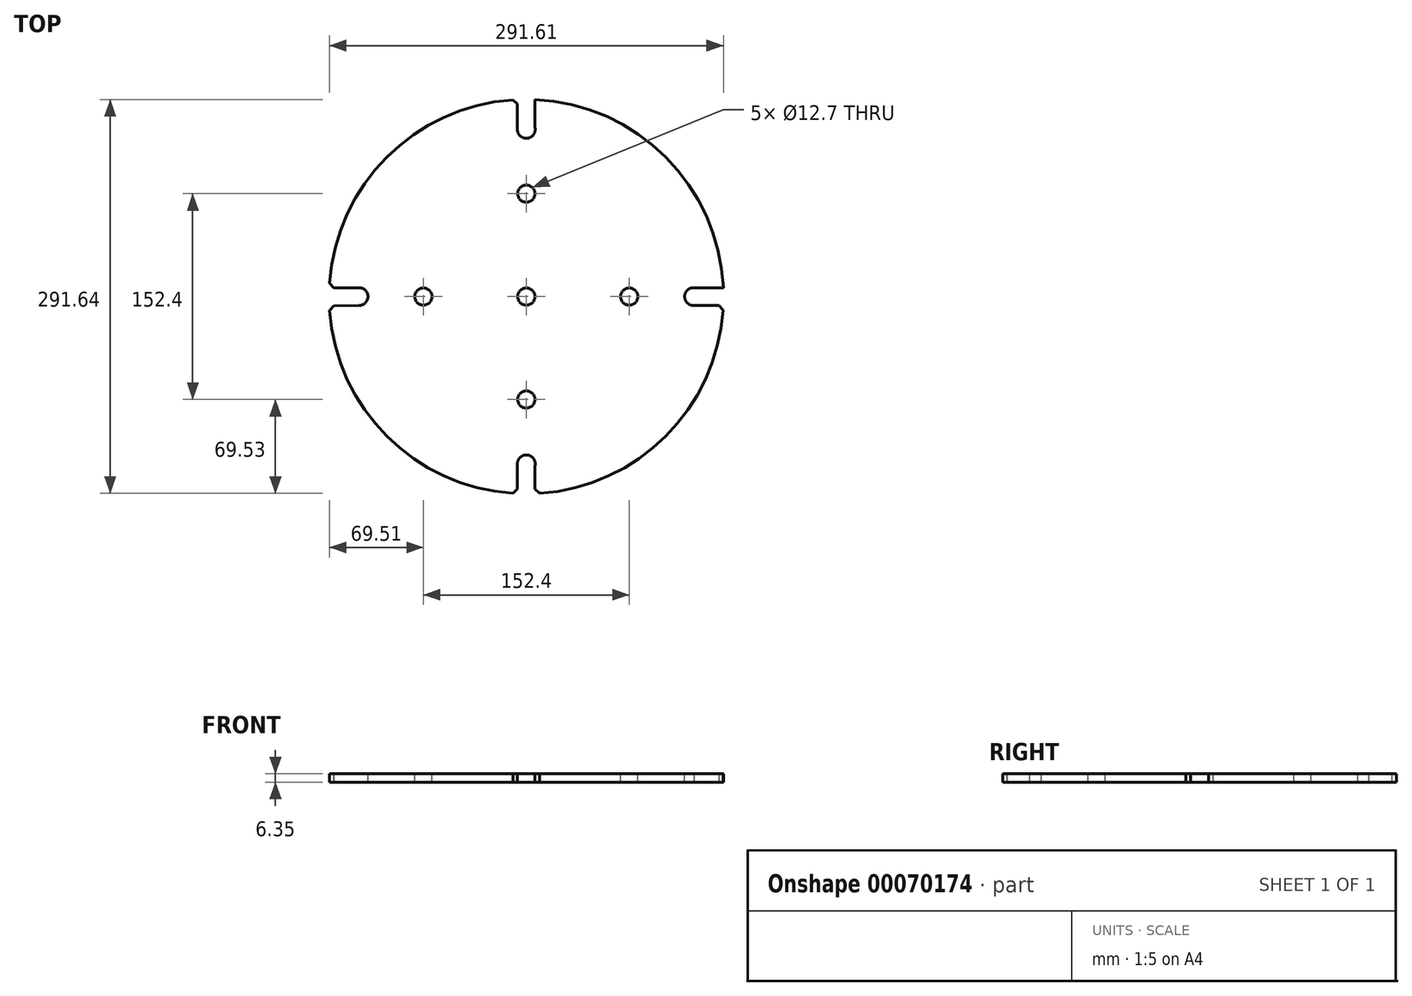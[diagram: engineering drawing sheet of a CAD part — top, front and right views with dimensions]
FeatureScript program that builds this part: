
annotation { "Feature Type Name" : "Feature", "Feature Type Description" : "" }
export const myFeature = defineFeature(function(context is Context, id is Id, definition is map)
    precondition{}
    {
        {
            var Q0;
            Q0=qCreatedBy(makeId("Top.planeOp"),FACE);
            var sketch = newSketch(context, id + "F0", { "sketchPlane" : qUnion([Q0])});
            skCircle(sketch, "E0", {"center": v(0, 0) * mm, "radius": 146.05 * mm});
            skSolve(sketch);
        }
        {
            var Q0;
            Q0 = qSketchRegion(id + "F0", true);
            extrude(context, id + "F1", {"entities" : qUnion([Q0]), "depth" : 6.35 * mm});
        }
        {
            var Q0;
            Q0=makeQuery(id+"F1.opExtrude","CAP_FACE",FACE,{"disambiguationData":[OSD([sQuery(id+"F0.wireOp",EDGE,"E0")])],"isStart":false});
            var sketch = newSketch(context, id + "F2", { "sketchPlane" : qUnion([Q0])});
            skCircle(sketch, "E1", {"center": v(0, 123.83) * mm, "radius": 6.6 * mm});
            skLineSegment(sketch, "E2", {"start": v(6.43, 125.34) * mm, "end": v(6.43, 145.9) * mm});
            skLineSegment(sketch, "E3", {"start": v(-6.6, 123.83) * mm, "end": v(-6.6, 145.9) * mm});
            skCircle(sketch, "E4", {"center": v(-123.83, 0) * mm, "radius": 6.6 * mm});
            skCircle(sketch, "E5", {"center": v(123.83, 0) * mm, "radius": 6.6 * mm});
            skCircle(sketch, "E6", {"center": v(0, -123.83) * mm, "radius": 6.6 * mm});
            skLineSegment(sketch, "E7", {"start": v(-123.8, 6.6) * mm, "end": v(-145.9, 6.6) * mm});
            skLineSegment(sketch, "E8", {"start": v(-123.74, -6.6) * mm, "end": v(-145.89, -6.88) * mm});
            skLineSegment(sketch, "E9", {"start": v(123.83, 6.6) * mm, "end": v(145.9, 6.6) * mm});
            skLineSegment(sketch, "E10", {"start": v(124.53, -6.57) * mm, "end": v(145.9, -6.57) * mm});
            skLineSegment(sketch, "E11", {"start": v(-6.6, -123.8) * mm, "end": v(-6.6, -145.9) * mm});
            skLineSegment(sketch, "E12", {"start": v(6.34, -125.67) * mm, "end": v(6.34, -145.91) * mm});
            skSolve(sketch);
        }
        {
            var Q0;
            {var subQ0=sQuery(id+"F2.wireOp",EDGE,"E1");var subQ1=makeQuery(id+"F2.imprint","INTERSECT",VERTEX,{"derivedFrom":[subQ0,sQuery(id+"F2.wireOp",EDGE,"E2")]});Q0=makeQuery(id+"F2.imprint","IMPRINT",FACE,{"disambiguationData":[TD([[makeQuery(id+"F2.imprint","IMPRINT",EDGE,{"disambiguationData":[TD([[subQ1,-1.0]])],"derivedFrom":subQ0}),1.0]])]});}
            var Q1;
            {var subQ0=sQuery(id+"F2.wireOp",EDGE,"E2");Q1=makeQuery(id+"F2.imprint","IMPRINT",FACE,{"disambiguationData":[TD([[makeQuery(id+"F2.imprint","IMPRINT",EDGE,{"derivedFrom":subQ0}),1.0]])]});}
            var Q2;
            {var subQ0=sQuery(id+"F2.wireOp",EDGE,"E4");var subQ1=makeQuery(id+"F2.imprint","INTERSECT",VERTEX,{"derivedFrom":[subQ0,sQuery(id+"F2.wireOp",EDGE,"E8")]});Q2=makeQuery(id+"F2.imprint","IMPRINT",FACE,{"disambiguationData":[TD([[makeQuery(id+"F2.imprint","IMPRINT",EDGE,{"disambiguationData":[TD([[subQ1,1.0]])],"derivedFrom":subQ0}),1.0]])]});}
            var Q3;
            {var subQ0=sQuery(id+"F2.wireOp",EDGE,"E8");Q3=makeQuery(id+"F2.imprint","IMPRINT",FACE,{"disambiguationData":[TD([[makeQuery(id+"F2.imprint","IMPRINT",EDGE,{"derivedFrom":subQ0}),-1.0]])]});}
            var Q4;
            {var subQ0=sQuery(id+"F2.wireOp",EDGE,"E6");var subQ1=makeQuery(id+"F2.imprint","INTERSECT",VERTEX,{"derivedFrom":[subQ0,sQuery(id+"F2.wireOp",EDGE,"E12")]});Q4=makeQuery(id+"F2.imprint","IMPRINT",FACE,{"disambiguationData":[TD([[makeQuery(id+"F2.imprint","IMPRINT",EDGE,{"disambiguationData":[TD([[subQ1,1.0]])],"derivedFrom":subQ0}),1.0]])]});}
            var Q5;
            {var subQ0=sQuery(id+"F2.wireOp",EDGE,"E12");Q5=makeQuery(id+"F2.imprint","IMPRINT",FACE,{"disambiguationData":[TD([[makeQuery(id+"F2.imprint","IMPRINT",EDGE,{"derivedFrom":subQ0}),-1.0]])]});}
            var Q6;
            {var subQ0=sQuery(id+"F2.wireOp",EDGE,"E5");var subQ1=makeQuery(id+"F2.imprint","INTERSECT",VERTEX,{"derivedFrom":[subQ0,sQuery(id+"F2.wireOp",EDGE,"E9")]});Q6=makeQuery(id+"F2.imprint","IMPRINT",FACE,{"disambiguationData":[TD([[makeQuery(id+"F2.imprint","IMPRINT",EDGE,{"disambiguationData":[TD([[subQ1,-1.0]])],"derivedFrom":subQ0}),1.0]])]});}
            var Q7;
            {var subQ0=sQuery(id+"F2.wireOp",EDGE,"E9");Q7=makeQuery(id+"F2.imprint","IMPRINT",FACE,{"disambiguationData":[TD([[makeQuery(id+"F2.imprint","IMPRINT",EDGE,{"derivedFrom":subQ0}),-1.0]])]});}
            extrude(context, id + "F3", {"entities" : qUnion([Q0, Q1, Q2, Q3, Q4, Q5, Q6, Q7]), "operationType" : NewBodyOperationType.REMOVE, "endBound" : BoundingType.THROUGH_ALL, "oppositeDirection" : true, "depth" : 25.4 * mm});
        }
        {
            var Q0;
            Q0=makeQuery(id+"F3.boolean.opBoolean","COPY",EDGE,{"derivedFrom":makeQuery(id+"F3.opExtrude","SWEPT_EDGE",EDGE,{"disambiguationData":[OSD([sQuery(id+"F0.wireOp",EDGE,"E0"),sQuery(id+"F2.wireOp",EDGE,"E3")])]})});
            var Q1;
            Q1=makeQuery(id+"F3.boolean.opBoolean","COPY",EDGE,{"derivedFrom":makeQuery(id+"F3.opExtrude","SWEPT_EDGE",EDGE,{"disambiguationData":[OSD([sQuery(id+"F0.wireOp",EDGE,"E0"),sQuery(id+"F2.wireOp",EDGE,"E2")])]})});
            var Q2;
            Q2=makeQuery(id+"F3.boolean.opBoolean","COPY",EDGE,{"derivedFrom":makeQuery(id+"F3.opExtrude","SWEPT_EDGE",EDGE,{"disambiguationData":[OSD([sQuery(id+"F0.wireOp",EDGE,"E0"),sQuery(id+"F2.wireOp",EDGE,"E7")])]})});
            var Q3;
            Q3=makeQuery(id+"F3.boolean.opBoolean","COPY",EDGE,{"derivedFrom":makeQuery(id+"F3.opExtrude","SWEPT_EDGE",EDGE,{"disambiguationData":[OSD([sQuery(id+"F0.wireOp",EDGE,"E0"),sQuery(id+"F2.wireOp",EDGE,"E8")])]})});
            var Q4;
            Q4=makeQuery(id+"F3.boolean.opBoolean","COPY",EDGE,{"derivedFrom":makeQuery(id+"F3.opExtrude","SWEPT_EDGE",EDGE,{"disambiguationData":[OSD([sQuery(id+"F0.wireOp",EDGE,"E0"),sQuery(id+"F2.wireOp",EDGE,"E11")])]})});
            var Q5;
            Q5=makeQuery(id+"F3.boolean.opBoolean","COPY",EDGE,{"derivedFrom":makeQuery(id+"F3.opExtrude","SWEPT_EDGE",EDGE,{"disambiguationData":[OSD([sQuery(id+"F0.wireOp",EDGE,"E0"),sQuery(id+"F2.wireOp",EDGE,"E12")])]})});
            var Q6;
            Q6=makeQuery(id+"F3.boolean.opBoolean","COPY",EDGE,{"derivedFrom":makeQuery(id+"F3.opExtrude","SWEPT_EDGE",EDGE,{"disambiguationData":[OSD([sQuery(id+"F0.wireOp",EDGE,"E0"),sQuery(id+"F2.wireOp",EDGE,"E9")])]})});
            var Q7;
            Q7=makeQuery(id+"F3.boolean.opBoolean","COPY",EDGE,{"derivedFrom":makeQuery(id+"F3.opExtrude","SWEPT_EDGE",EDGE,{"disambiguationData":[OSD([sQuery(id+"F0.wireOp",EDGE,"E0"),sQuery(id+"F2.wireOp",EDGE,"E10")])]})});
            chamfer(context, id + "F4", {"entities" : qUnion([Q0, Q1, Q2, Q3, Q4, Q5, Q6, Q7]), "width" : 3.17 * mm, "tangentPropagation" : true});
        }
        {
            var Q0;
            Q0=makeQuery(id+"F1.opExtrude","CAP_FACE",FACE,{"disambiguationData":[OSD([sQuery(id+"F0.wireOp",EDGE,"E0")])],"isStart":false});
            var sketch = newSketch(context, id + "F5", { "sketchPlane" : qUnion([Q0])});
            skCircle(sketch, "E13", {"center": v(0, 0) * mm, "radius": 6.35 * mm});
            skSolve(sketch);
        }
        {
            var Q0;
            Q0 = qSketchRegion(id + "F5", true);
            extrude(context, id + "F6", {"entities" : qUnion([Q0]), "operationType" : NewBodyOperationType.REMOVE, "endBound" : BoundingType.THROUGH_ALL, "oppositeDirection" : true, "depth" : 25.4 * mm});
        }
        {
            var Q0;
            Q0=makeQuery(id+"F1.opExtrude","CAP_FACE",FACE,{"disambiguationData":[OSD([sQuery(id+"F0.wireOp",EDGE,"E0")])],"isStart":false});
            var sketch = newSketch(context, id + "F7", { "sketchPlane" : qUnion([Q0])});
            skCircle(sketch, "E14", {"center": v(76.2, 0) * mm, "radius": 6.35 * mm});
            skCircle(sketch, "E15", {"center": v(0, 76.2) * mm, "radius": 6.35 * mm});
            skCircle(sketch, "E16", {"center": v(-76.2, 0) * mm, "radius": 6.35 * mm});
            skCircle(sketch, "E17", {"center": v(0, -76.2) * mm, "radius": 6.35 * mm});
            skSolve(sketch);
        }
        {
            var Q0;
            Q0 = qSketchRegion(id + "F7", true);
            extrude(context, id + "F8", {"entities" : qUnion([Q0]), "operationType" : NewBodyOperationType.REMOVE, "endBound" : BoundingType.THROUGH_ALL, "oppositeDirection" : true, "depth" : 25.4 * mm});
        }
    });
